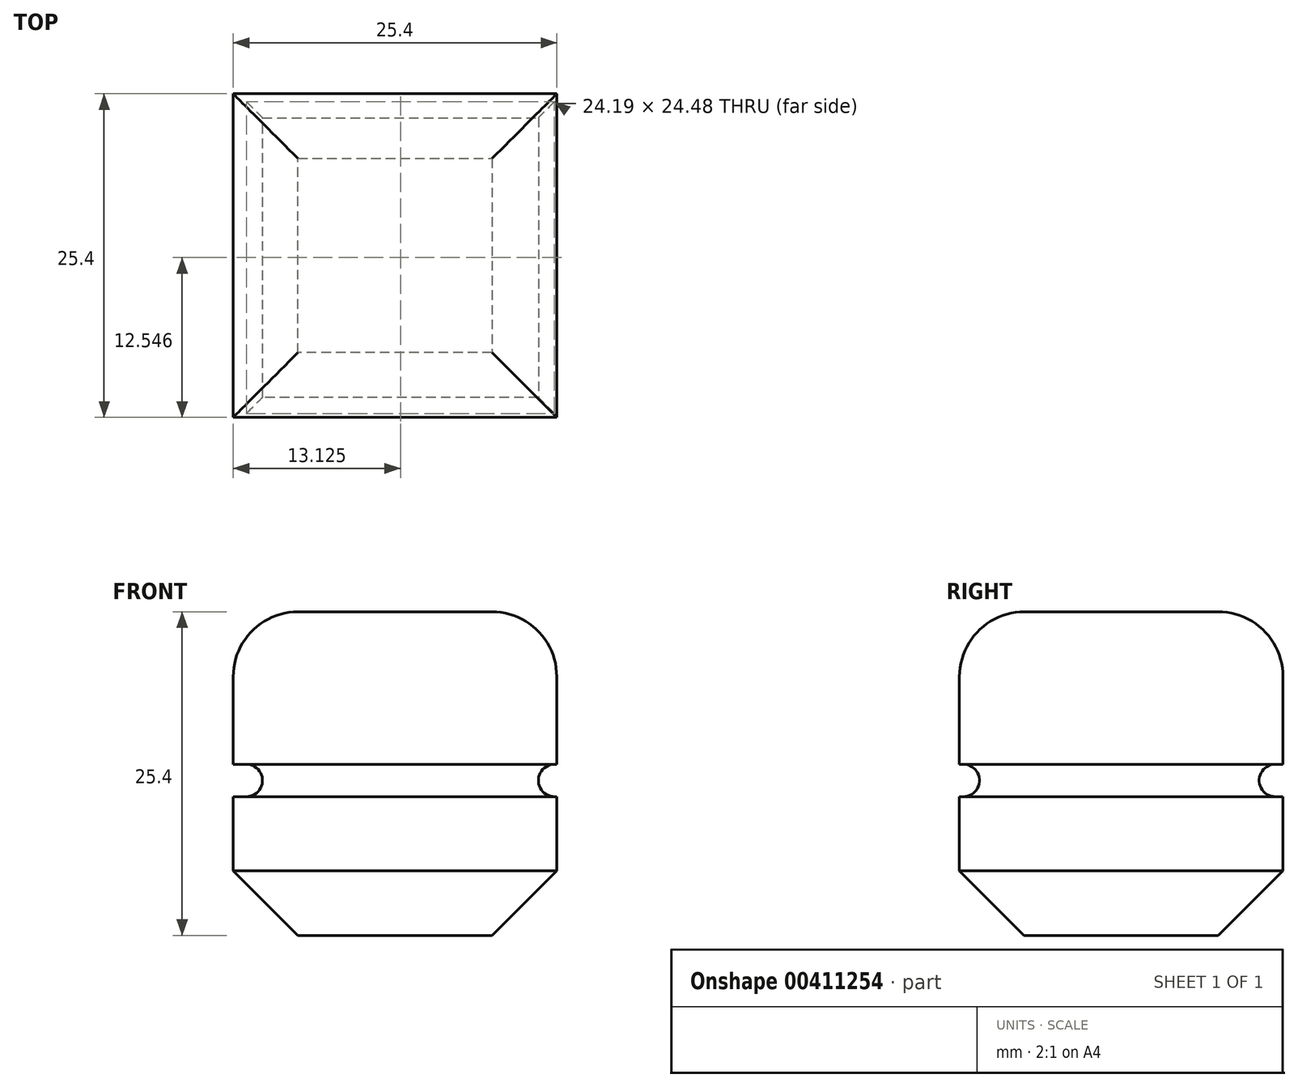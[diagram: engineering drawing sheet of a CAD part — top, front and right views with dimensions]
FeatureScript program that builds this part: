
annotation { "Feature Type Name" : "Feature", "Feature Type Description" : "" }
export const myFeature = defineFeature(function(context is Context, id is Id, definition is map)
    precondition{}
    {
        {
            var Q0;
            Q0=qCreatedBy(makeId("Front.planeOp"),FACE);
            var sketch = newSketch(context, id + "F0", { "sketchPlane" : qUnion([Q0])});
            skLineSegment(sketch, "E0.bottom", {"start": v(-61.54, 11.97) * mm, "end": v(-36.14, 11.97) * mm});
            skLineSegment(sketch, "E0.top", {"start": v(-61.54, -13.43) * mm, "end": v(-36.14, -13.43) * mm});
            skLineSegment(sketch, "E0.left", {"start": v(-61.54, 11.97) * mm, "end": v(-61.54, -13.43) * mm});
            skLineSegment(sketch, "E0.right", {"start": v(-36.14, 11.97) * mm, "end": v(-36.14, -13.43) * mm});
            skSolve(sketch);
        }
        {
            var Q0;
            Q0=makeQuery(id+"F0.imprint","IMPRINT",FACE,{"disambiguationData":[TD([[makeQuery(id+"F0.imprint","IMPRINT",EDGE,{"derivedFrom":sQuery(id+"F0.wireOp",EDGE,"E0.bottom")}),-1.0]])]});
            extrude(context, id + "F1", {"entities" : qUnion([Q0]), "depth" : 25.4 * mm});
        }
        {
            var Q0;
            Q0=makeQuery(id+"F1.opExtrude","CAP_EDGE",EDGE,{"disambiguationData":[OSD([sQuery(id+"F0.wireOp",EDGE,"E0.bottom")])],"isStart":false});
            var Q1;
            Q1=makeQuery(id+"F1.opExtrude","SWEPT_EDGE",EDGE,{"disambiguationData":[OSD([sQuery(id+"F0.wireOp",EDGE,"E0.bottom"),sQuery(id+"F0.wireOp",EDGE,"E0.right")])]});
            var Q2;
            Q2=makeQuery(id+"F1.opExtrude","CAP_EDGE",EDGE,{"disambiguationData":[OSD([sQuery(id+"F0.wireOp",EDGE,"E0.bottom")])],"isStart":true});
            var Q3;
            Q3=makeQuery(id+"F1.opExtrude","SWEPT_EDGE",EDGE,{"disambiguationData":[OSD([sQuery(id+"F0.wireOp",EDGE,"E0.bottom"),sQuery(id+"F0.wireOp",EDGE,"E0.left")])]});
            fillet(context, id + "F2", {"entities" : qUnion([Q0, Q1, Q2, Q3]), "radius" : 5.08 * mm, "tangentPropagation" : true, "allowEdgeOverflow" : false});
        }
        {
            var Q0;
            Q0=makeQuery(id+"F1.opExtrude","CAP_EDGE",EDGE,{"disambiguationData":[OSD([sQuery(id+"F0.wireOp",EDGE,"E0.top")])],"isStart":false});
            var Q1;
            Q1=makeQuery(id+"F1.opExtrude","SWEPT_EDGE",EDGE,{"disambiguationData":[OSD([sQuery(id+"F0.wireOp",EDGE,"E0.top"),sQuery(id+"F0.wireOp",EDGE,"E0.right")])]});
            var Q2;
            Q2=makeQuery(id+"F1.opExtrude","SWEPT_EDGE",EDGE,{"disambiguationData":[OSD([sQuery(id+"F0.wireOp",EDGE,"E0.top"),sQuery(id+"F0.wireOp",EDGE,"E0.left")])]});
            var Q3;
            Q3=makeQuery(id+"F1.opExtrude","CAP_EDGE",EDGE,{"disambiguationData":[OSD([sQuery(id+"F0.wireOp",EDGE,"E0.top")])],"isStart":true});
            chamfer(context, id + "F3", {"entities" : qUnion([Q0, Q1, Q2, Q3]), "width" : 5.08 * mm, "tangentPropagation" : true});
        }
        {
            var Q0;
            Q0=qCreatedBy(makeId("Top.planeOp"),FACE);
            var sketch = newSketch(context, id + "F4", { "sketchPlane" : qUnion([Q0])});
            skLineSegment(sketch, "E1.bottom", {"start": v(-35.84, -25.58) * mm, "end": v(-61.58, -25.58) * mm});
            skLineSegment(sketch, "E1.top", {"start": v(-35.84, 0) * mm, "end": v(-61.58, 0) * mm});
            skLineSegment(sketch, "E1.left", {"start": v(-35.84, -25.58) * mm, "end": v(-35.84, 0) * mm});
            skLineSegment(sketch, "E1.right", {"start": v(-61.58, -25.58) * mm, "end": v(-61.58, 0) * mm});
            skLineSegment(sketch, "E2.bottom", {"start": v(-37.6, -23.82) * mm, "end": v(-59.24, -23.82) * mm});
            skLineSegment(sketch, "E2.top", {"start": v(-37.6, -1.88) * mm, "end": v(-59.24, -1.88) * mm});
            skLineSegment(sketch, "E2.left", {"start": v(-37.6, -23.82) * mm, "end": v(-37.6, -1.88) * mm});
            skLineSegment(sketch, "E2.right", {"start": v(-59.24, -23.82) * mm, "end": v(-59.24, -1.88) * mm});
            skSolve(sketch);
        }
        {
            var Q0;
            Q0=makeQuery(id+"F4.imprint","IMPRINT",FACE,{"disambiguationData":[TD([[makeQuery(id+"F4.imprint","IMPRINT",EDGE,{"derivedFrom":sQuery(id+"F4.wireOp",EDGE,"E1.bottom")}),-1.0]])]});
            extrude(context, id + "F5", {"entities" : qUnion([Q0]), "operationType" : NewBodyOperationType.REMOVE, "oppositeDirection" : true, "depth" : 2.54 * mm});
        }
        {
            var Q0;
            Q0=makeQuery(id+"F5.boolean.opBoolean","COPY",EDGE,{"derivedFrom":makeQuery(id+"F5.opExtrude","CAP_EDGE",EDGE,{"disambiguationData":[OSD([sQuery(id+"F4.wireOp",EDGE,"E2.top")])],"isStart":false})});
            var Q1;
            Q1=makeQuery(id+"F5.boolean.opBoolean","COPY",EDGE,{"derivedFrom":makeQuery(id+"F5.opExtrude","CAP_EDGE",EDGE,{"disambiguationData":[OSD([sQuery(id+"F4.wireOp",EDGE,"E2.left")])],"isStart":false})});
            var Q2;
            Q2=makeQuery(id+"F5.boolean.opBoolean","COPY",EDGE,{"derivedFrom":makeQuery(id+"F5.opExtrude","CAP_EDGE",EDGE,{"disambiguationData":[OSD([sQuery(id+"F4.wireOp",EDGE,"E2.top")])],"isStart":true})});
            var Q3;
            Q3=makeQuery(id+"F5.boolean.opBoolean","COPY",EDGE,{"derivedFrom":makeQuery(id+"F5.opExtrude","CAP_EDGE",EDGE,{"disambiguationData":[OSD([sQuery(id+"F4.wireOp",EDGE,"E2.left")])],"isStart":true})});
            var Q4;
            Q4=makeQuery(id+"F5.boolean.opBoolean","COPY",EDGE,{"derivedFrom":makeQuery(id+"F5.opExtrude","CAP_EDGE",EDGE,{"disambiguationData":[OSD([sQuery(id+"F4.wireOp",EDGE,"E2.bottom")])],"isStart":false})});
            var Q5;
            Q5=makeQuery(id+"F5.boolean.opBoolean","COPY",EDGE,{"derivedFrom":makeQuery(id+"F5.opExtrude","CAP_EDGE",EDGE,{"disambiguationData":[OSD([sQuery(id+"F4.wireOp",EDGE,"E2.right")])],"isStart":false})});
            var Q6;
            Q6=makeQuery(id+"F5.boolean.opBoolean","COPY",EDGE,{"derivedFrom":makeQuery(id+"F5.opExtrude","CAP_EDGE",EDGE,{"disambiguationData":[OSD([sQuery(id+"F4.wireOp",EDGE,"E2.bottom")])],"isStart":true})});
            var Q7;
            Q7=makeQuery(id+"F5.boolean.opBoolean","COPY",EDGE,{"derivedFrom":makeQuery(id+"F5.opExtrude","CAP_EDGE",EDGE,{"disambiguationData":[OSD([sQuery(id+"F4.wireOp",EDGE,"E2.right")])],"isStart":true})});
            fillet(context, id + "F6", {"entities" : qUnion([Q0, Q1, Q2, Q3, Q4, Q5, Q6, Q7]), "radius" : 1.27 * mm, "tangentPropagation" : true, "allowEdgeOverflow" : false});
        }
    });
